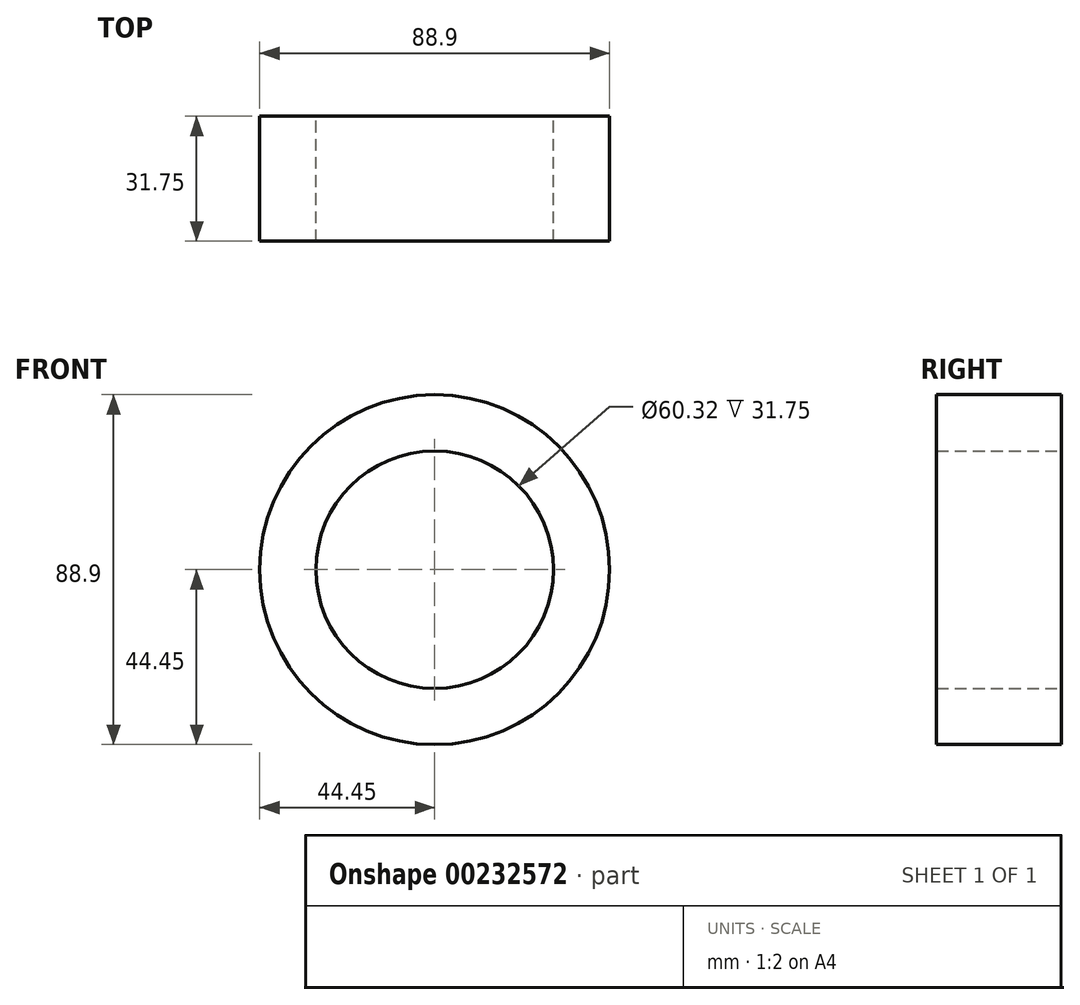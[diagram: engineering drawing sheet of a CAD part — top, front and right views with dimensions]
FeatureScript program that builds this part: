
annotation { "Feature Type Name" : "Feature", "Feature Type Description" : "" }
export const myFeature = defineFeature(function(context is Context, id is Id, definition is map)
    precondition{}
    {
        {
            var Q0;
            Q0=qCreatedBy(makeId("Front.planeOp"),FACE);
            var sketch = newSketch(context, id + "F0", { "sketchPlane" : qUnion([Q0])});
            skCircle(sketch, "E0", {"center": v(0, 0) * mm, "radius": 44.45 * mm});
            skCircle(sketch, "E1", {"center": v(0, 0) * mm, "radius": 30.16 * mm});
            skLineSegment(sketch, "E2", {"start": v(-30.16, 56.63) * mm, "end": v(-33.17, 57.61) * mm, "construction": true});
            skSolve(sketch);
        }
        {
            var Q0;
            Q0=makeQuery(id+"F0.imprint","IMPRINT",FACE,{"disambiguationData":[TD([[makeQuery(id+"F0.imprint","IMPRINT",EDGE,{"derivedFrom":sQuery(id+"F0.wireOp",EDGE,"E0")}),1.0]])]});
            extrude(context, id + "F1", {"entities" : qUnion([Q0]), "depth" : 31.75 * mm});
        }
    });
